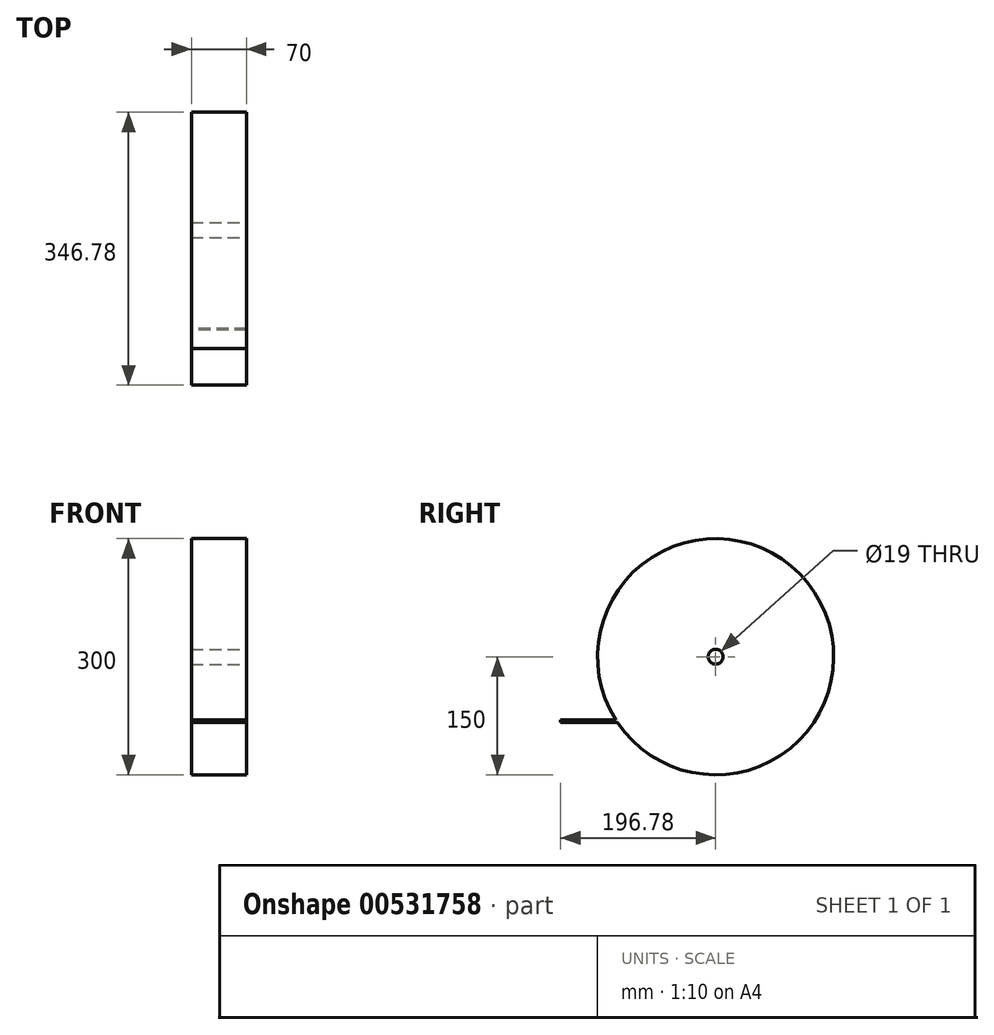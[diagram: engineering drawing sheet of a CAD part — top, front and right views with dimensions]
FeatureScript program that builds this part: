
annotation { "Feature Type Name" : "Feature", "Feature Type Description" : "" }
export const myFeature = defineFeature(function(context is Context, id is Id, definition is map)
    precondition{}
    {
        {
            var Q0;
            Q0=qCreatedBy(makeId("Right.planeOp"),FACE);
            var sketch = newSketch(context, id + "F0", { "sketchPlane" : qUnion([Q0])});
            skCircle(sketch, "E0", {"center": v(0, 0) * mm, "radius": 150 * mm});
            skSolve(sketch);
        }
        {
            var Q0;
            Q0 = qSketchRegion(id + "F0", true);
            extrude(context, id + "F1", {"entities" : qUnion([Q0]), "depth" : 70 * mm, "offsetDistance" : 25 * mm});
        }
        {
            var Q0;
            Q0=qCreatedBy(makeId("Front.planeOp"),FACE);
            var sketch = newSketch(context, id + "F2", { "sketchPlane" : qUnion([Q0])});
            skLineSegment(sketch, "E1", {"start": v(0, 0) * mm, "end": v(0, -80.23) * mm});
            skLineSegment(sketch, "E2", {"start": v(0, -80.23) * mm, "end": v(70, -80.23) * mm});
            skLineSegment(sketch, "E3", {"start": v(70, -80.23) * mm, "end": v(70, -83.23) * mm});
            skLineSegment(sketch, "E4", {"start": v(70, -83.23) * mm, "end": v(0, -83.23) * mm});
            skLineSegment(sketch, "E5", {"start": v(0, -83.23) * mm, "end": v(0, -80.23) * mm});
            skSolve(sketch);
        }
        {
            var Q0;
            Q0 = qSketchRegion(id + "F2", true);
            extrude(context, id + "F3", {"entities" : qUnion([Q0]), "operationType" : NewBodyOperationType.ADD, "depth" : 196.78 * mm, "offsetDistance" : 25 * mm});
        }
        {
            var Q0;
            Q0=makeQuery(id+"F3.boolean.opBoolean","MERGE",FACE,{"derivedFrom":[makeQuery(id+"F1.opExtrude","CAP_FACE",FACE,{"disambiguationData":[OSD([sQuery(id+"F0.wireOp",EDGE,"E0")])],"isStart":false}),makeQuery(id+"F3.opExtrude","SWEPT_FACE",FACE,{"disambiguationData":[OSD([sQuery(id+"F2.wireOp",EDGE,"E3")])]})]});
            var sketch = newSketch(context, id + "F4", { "sketchPlane" : qUnion([Q0])});
            skCircle(sketch, "E6", {"center": v(0, 0) * mm, "radius": 9.5 * mm});
            skSolve(sketch);
        }
        {
            var Q0;
            Q0 = qSketchRegion(id + "F4", true);
            extrude(context, id + "F5", {"entities" : qUnion([Q0]), "operationType" : NewBodyOperationType.REMOVE, "oppositeDirection" : true, "depth" : 184 * mm, "offsetDistance" : 25 * mm});
        }
    });
